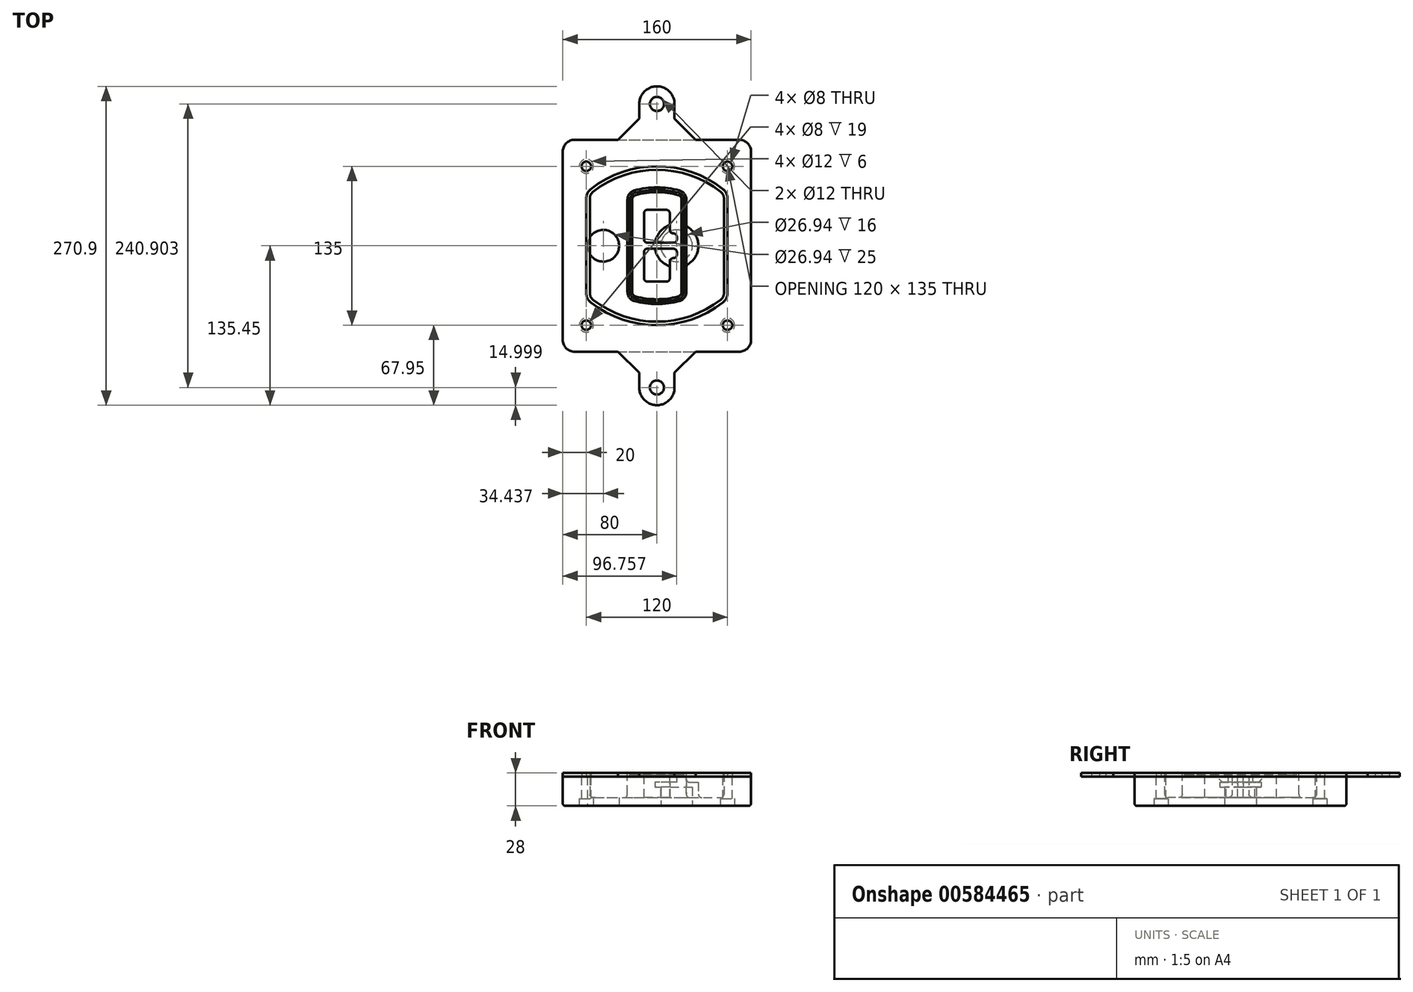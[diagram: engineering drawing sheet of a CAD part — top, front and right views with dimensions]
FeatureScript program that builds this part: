
annotation { "Feature Type Name" : "Feature", "Feature Type Description" : "" }
export const myFeature = defineFeature(function(context is Context, id is Id, definition is map)
    precondition{}
    {
        {
            var Q0;
            Q0=qCreatedBy(makeId("Top.planeOp"),FACE);
            var sketch = newSketch(context, id + "F0", { "sketchPlane" : qUnion([Q0])});
            skPoint(sketch, "E0.rect.middle", {"position": v(0, 0) * mm});
            skLineSegment(sketch, "E1.bottom", {"start": v(-70, -90) * mm, "end": v(70, -90) * mm});
            skLineSegment(sketch, "E1.top", {"start": v(-70, 90) * mm, "end": v(70, 90) * mm});
            skLineSegment(sketch, "E1.left", {"start": v(-80, -80) * mm, "end": v(-80, 80) * mm});
            skLineSegment(sketch, "E1.right", {"start": v(80, -80) * mm, "end": v(80, 80) * mm});
            skLineSegment(sketch, "E2", {"start": v(-80, 90) * mm, "end": v(80, -90) * mm, "construction": true});
            skLineSegment(sketch, "E3", {"start": v(80, 90) * mm, "end": v(-80, -90) * mm, "construction": true});
            skCircle(sketch, "E4", {"center": v(-60, 67.5) * mm, "radius": 4 * mm});
            skCircle(sketch, "E5", {"center": v(60, 67.5) * mm, "radius": 4 * mm});
            skCircle(sketch, "E6", {"center": v(60, -67.5) * mm, "radius": 4 * mm});
            skCircle(sketch, "E7", {"center": v(-60, -67.5) * mm, "radius": 4 * mm});
            skLineSegment(sketch, "E8", {"start": v(-60, 67.5) * mm, "end": v(60, 67.5) * mm, "construction": true});
            skLineSegment(sketch, "E9", {"start": v(60, 67.5) * mm, "end": v(60, -67.5) * mm, "construction": true});
            skLineSegment(sketch, "E10", {"start": v(60, -67.5) * mm, "end": v(-60, -67.5) * mm, "construction": true});
            skLineSegment(sketch, "E11", {"start": v(-60, -67.5) * mm, "end": v(-60, 67.5) * mm, "construction": true});
            skLineSegment(sketch, "E12", {"start": v(-60, 40.3) * mm, "end": v(-60, -40.3) * mm});
            skLineSegment(sketch, "E13", {"start": v(60, 40.3) * mm, "end": v(60, -40.3) * mm});
            skArc(sketch, "E14", {"start": v(56.15, 48.18) * mm, "mid": v(0, 67.5) * mm, "end": v(-56.15, 48.18) * mm});
            skArc(sketch, "E15", {"start": v(-56.15, -48.18) * mm, "mid": v(0, -67.5) * mm, "end": v(56.15, -48.18) * mm});
            skLineSegment(sketch, "E16", {"start": v(-60, 0) * mm, "end": v(60, 0) * mm, "construction": true});
            skPoint(sketch, "E17.visualSharp", {"position": v(-60, -45) * mm});
            skArc(sketch, "E17.filletArc", {"start": v(-60, -40.3) * mm, "mid": v(-58.99, -44.68) * mm, "end": v(-56.15, -48.18) * mm});
            skPoint(sketch, "E18.visualSharp", {"position": v(-60, 45) * mm});
            skArc(sketch, "E18.filletArc", {"start": v(-56.15, 48.18) * mm, "mid": v(-58.99, 44.68) * mm, "end": v(-60, 40.3) * mm});
            skPoint(sketch, "E19.visualSharp", {"position": v(60, 45) * mm});
            skArc(sketch, "E19.filletArc", {"start": v(60, 40.3) * mm, "mid": v(58.99, 44.68) * mm, "end": v(56.15, 48.18) * mm});
            skPoint(sketch, "E20.visualSharp", {"position": v(60, -45) * mm});
            skArc(sketch, "E20.filletArc", {"start": v(56.15, -48.18) * mm, "mid": v(58.99, -44.68) * mm, "end": v(60, -40.3) * mm});
            skPoint(sketch, "E21.visualSharp", {"position": v(-80, 90) * mm});
            skArc(sketch, "E21.filletArc", {"start": v(-70, 90) * mm, "mid": v(-77.07, 87.07) * mm, "end": v(-80, 80) * mm});
            skPoint(sketch, "E22.visualSharp", {"position": v(80, 90) * mm});
            skArc(sketch, "E22.filletArc", {"start": v(80, 80) * mm, "mid": v(77.07, 87.07) * mm, "end": v(70, 90) * mm});
            skPoint(sketch, "E23.visualSharp", {"position": v(80, -90) * mm});
            skArc(sketch, "E23.filletArc", {"start": v(70, -90) * mm, "mid": v(77.07, -87.07) * mm, "end": v(80, -80) * mm});
            skPoint(sketch, "E24.visualSharp", {"position": v(-80, -90) * mm});
            skArc(sketch, "E24.filletArc", {"start": v(-80, -80) * mm, "mid": v(-77.07, -87.07) * mm, "end": v(-70, -90) * mm});
            skArc(sketch, "E25.0", {"start": v(57, 40.3) * mm, "mid": v(56.3, 43.36) * mm, "end": v(54.3, 45.81) * mm});
            skLineSegment(sketch, "E25.1", {"start": v(57, 40.3) * mm, "end": v(57, -40.3) * mm});
            skArc(sketch, "E25.2", {"start": v(54.3, -45.81) * mm, "mid": v(56.3, -43.36) * mm, "end": v(57, -40.3) * mm});
            skArc(sketch, "E25.3", {"start": v(-54.3, -45.81) * mm, "mid": v(0, -64.5) * mm, "end": v(54.3, -45.81) * mm});
            skArc(sketch, "E25.4", {"start": v(-57, -40.3) * mm, "mid": v(-56.3, -43.36) * mm, "end": v(-54.3, -45.81) * mm});
            skArc(sketch, "E25.5", {"start": v(54.3, 45.81) * mm, "mid": v(0, 64.5) * mm, "end": v(-54.3, 45.81) * mm});
            skLineSegment(sketch, "E25.6", {"start": v(-57, 40.3) * mm, "end": v(-57, -40.3) * mm});
            skArc(sketch, "E25.7", {"start": v(-54.3, 45.81) * mm, "mid": v(-56.3, 43.36) * mm, "end": v(-57, 40.3) * mm});
            skArc(sketch, "E26.0", {"start": v(-58.62, 51.33) * mm, "mid": v(-62.58, 46.43) * mm, "end": v(-64, 40.3) * mm});
            skArc(sketch, "E26.1", {"start": v(58.62, 51.33) * mm, "mid": v(0, 71.5) * mm, "end": v(-58.62, 51.33) * mm});
            skArc(sketch, "E26.2", {"start": v(64, 40.3) * mm, "mid": v(62.58, 46.43) * mm, "end": v(58.62, 51.33) * mm});
            skLineSegment(sketch, "E26.3", {"start": v(64, 40.3) * mm, "end": v(64, -40.3) * mm});
            skArc(sketch, "E26.4", {"start": v(58.62, -51.33) * mm, "mid": v(62.58, -46.43) * mm, "end": v(64, -40.3) * mm});
            skLineSegment(sketch, "E26.5", {"start": v(-64, 40.3) * mm, "end": v(-64, -40.3) * mm});
            skArc(sketch, "E26.6", {"start": v(-58.62, -51.33) * mm, "mid": v(0, -71.5) * mm, "end": v(58.62, -51.33) * mm});
            skArc(sketch, "E26.7", {"start": v(-64, -40.3) * mm, "mid": v(-62.58, -46.43) * mm, "end": v(-58.62, -51.33) * mm});
            skSolve(sketch);
        }
        {
            var Q0;
            Q0=makeQuery(id+"F0.imprint","IMPRINT",FACE,{"disambiguationData":[TD([[makeQuery(id+"F0.imprint","IMPRINT",EDGE,{"derivedFrom":sQuery(id+"F0.wireOp",EDGE,"E1.bottom")}),1.0]])]});
            var Q1;
            Q1=makeQuery(id+"F0.imprint","IMPRINT",FACE,{"disambiguationData":[TD([[makeQuery(id+"F0.imprint","IMPRINT",EDGE,{"derivedFrom":sQuery(id+"F0.wireOp",EDGE,"E12")}),1.0]])]});
            var Q2;
            Q2=makeQuery(id+"F0.imprint","IMPRINT",FACE,{"disambiguationData":[TD([[makeQuery(id+"F0.imprint","IMPRINT",EDGE,{"derivedFrom":sQuery(id+"F0.wireOp",EDGE,"E25.0")}),1.0]])]});
            var Q3;
            Q3=makeQuery(id+"F0.imprint","IMPRINT",FACE,{"disambiguationData":[TD([[makeQuery(id+"F0.imprint","IMPRINT",EDGE,{"derivedFrom":sQuery(id+"F0.wireOp",EDGE,"E12")}),-1.0]])]});
            extrude(context, id + "F1", {"entities" : qUnion([Q0, Q1, Q2, Q3]), "oppositeDirection" : true, "depth" : 25 * mm});
        }
        {
            var Q0;
            Q0=makeQuery(id+"F0.imprint","IMPRINT",FACE,{"disambiguationData":[TD([[makeQuery(id+"F0.imprint","IMPRINT",EDGE,{"derivedFrom":sQuery(id+"F0.wireOp",EDGE,"E12")}),1.0]])]});
            extrude(context, id + "F2", {"entities" : qUnion([Q0]), "operationType" : NewBodyOperationType.ADD, "depth" : 3 * mm});
        }
        {
            var Q0;
            Q0=makeQuery(id+"F0.imprint","IMPRINT",FACE,{"disambiguationData":[TD([[makeQuery(id+"F0.imprint","IMPRINT",EDGE,{"derivedFrom":sQuery(id+"F0.wireOp",EDGE,"E25.0")}),1.0]])]});
            extrude(context, id + "F3", {"entities" : qUnion([Q0]), "operationType" : NewBodyOperationType.REMOVE, "oppositeDirection" : true, "depth" : 18 * mm});
        }
        {
            var Q0;
            Q0=makeQuery(id+"F2.opExtrude","CAP_FACE",FACE,{"disambiguationData":[OSD([sQuery(id+"F0.wireOp",EDGE,"E12"),sQuery(id+"F0.wireOp",EDGE,"E13"),sQuery(id+"F0.wireOp",EDGE,"E14"),sQuery(id+"F0.wireOp",EDGE,"E15"),sQuery(id+"F0.wireOp",EDGE,"E17.filletArc"),sQuery(id+"F0.wireOp",EDGE,"E18.filletArc"),sQuery(id+"F0.wireOp",EDGE,"E19.filletArc"),sQuery(id+"F0.wireOp",EDGE,"E20.filletArc"),sQuery(id+"F0.wireOp",EDGE,"E25.0"),sQuery(id+"F0.wireOp",EDGE,"E25.1"),sQuery(id+"F0.wireOp",EDGE,"E25.2"),sQuery(id+"F0.wireOp",EDGE,"E25.3"),sQuery(id+"F0.wireOp",EDGE,"E25.4"),sQuery(id+"F0.wireOp",EDGE,"E25.5"),sQuery(id+"F0.wireOp",EDGE,"E25.6"),sQuery(id+"F0.wireOp",EDGE,"E25.7")])],"isStart":false});
            var sketch = newSketch(context, id + "F4", { "sketchPlane" : qUnion([Q0])});
            skArc(sketch, "E27.0", {"start": v(-19.08, -46.97) * mm, "mid": v(0, -49.5) * mm, "end": v(19.08, -46.97) * mm});
            skArc(sketch, "E28.0", {"start": v(19.08, 46.97) * mm, "mid": v(0, 49.5) * mm, "end": v(-19.08, 46.97) * mm});
            skLineSegment(sketch, "E29", {"start": v(-25, 39.25) * mm, "end": v(-25, -39.25) * mm});
            skLineSegment(sketch, "E30", {"start": v(25, 39.25) * mm, "end": v(25, -39.25) * mm});
            skLineSegment(sketch, "E31", {"start": v(-25, 45.1) * mm, "end": v(25, 45.1) * mm, "construction": true});
            skLineSegment(sketch, "E32", {"start": v(-25, -45.1) * mm, "end": v(25, -45.1) * mm, "construction": true});
            skPoint(sketch, "E33.visualSharp", {"position": v(-25, 45.1) * mm});
            skArc(sketch, "E33.filletArc", {"start": v(-19.08, 46.97) * mm, "mid": v(-23.35, 44.11) * mm, "end": v(-25, 39.25) * mm});
            skPoint(sketch, "E34.visualSharp", {"position": v(25, 45.1) * mm});
            skArc(sketch, "E34.filletArc", {"start": v(25, 39.25) * mm, "mid": v(23.35, 44.11) * mm, "end": v(19.08, 46.97) * mm});
            skPoint(sketch, "E35.visualSharp", {"position": v(25, -45.1) * mm});
            skArc(sketch, "E35.filletArc", {"start": v(19.08, -46.97) * mm, "mid": v(23.35, -44.11) * mm, "end": v(25, -39.25) * mm});
            skPoint(sketch, "E36.visualSharp", {"position": v(-25, -45.1) * mm});
            skArc(sketch, "E36.filletArc", {"start": v(-25, -39.25) * mm, "mid": v(-23.35, -44.11) * mm, "end": v(-19.08, -46.97) * mm});
            skArc(sketch, "E37.0", {"start": v(54.3, 45.81) * mm, "mid": v(0, 64.5) * mm, "end": v(-54.3, 45.81) * mm});
            skArc(sketch, "E37.1", {"start": v(-54.3, 45.81) * mm, "mid": v(-56.3, 43.36) * mm, "end": v(-57, 40.3) * mm});
            skLineSegment(sketch, "E37.2", {"start": v(-57, 40.3) * mm, "end": v(-57, -40.3) * mm});
            skArc(sketch, "E37.3", {"start": v(-57, -40.3) * mm, "mid": v(-56.3, -43.36) * mm, "end": v(-54.3, -45.81) * mm});
            skArc(sketch, "E37.4", {"start": v(-54.3, -45.81) * mm, "mid": v(0, -64.5) * mm, "end": v(54.3, -45.81) * mm});
            skArc(sketch, "E37.5", {"start": v(54.3, -45.81) * mm, "mid": v(56.3, -43.36) * mm, "end": v(57, -40.3) * mm});
            skLineSegment(sketch, "E37.6", {"start": v(57, 40.3) * mm, "end": v(57, -40.3) * mm});
            skArc(sketch, "E37.7", {"start": v(57, 40.3) * mm, "mid": v(56.3, 43.36) * mm, "end": v(54.3, 45.81) * mm});
            skLineSegment(sketch, "E38.0", {"start": v(23, 39.25) * mm, "end": v(23, -39.25) * mm});
            skArc(sketch, "E38.1", {"start": v(18.56, -45.04) * mm, "mid": v(21.76, -42.9) * mm, "end": v(23, -39.25) * mm});
            skArc(sketch, "E38.2", {"start": v(-18.56, -45.04) * mm, "mid": v(0, -47.5) * mm, "end": v(18.56, -45.04) * mm});
            skArc(sketch, "E38.3", {"start": v(-23, -39.25) * mm, "mid": v(-21.76, -42.9) * mm, "end": v(-18.56, -45.04) * mm});
            skLineSegment(sketch, "E38.4", {"start": v(-23, 39.25) * mm, "end": v(-23, -39.25) * mm});
            skArc(sketch, "E38.5", {"start": v(23, 39.25) * mm, "mid": v(21.76, 42.9) * mm, "end": v(18.56, 45.04) * mm});
            skArc(sketch, "E38.6", {"start": v(-18.56, 45.04) * mm, "mid": v(-21.76, 42.9) * mm, "end": v(-23, 39.25) * mm});
            skArc(sketch, "E38.7", {"start": v(18.56, 45.04) * mm, "mid": v(0, 47.5) * mm, "end": v(-18.56, 45.04) * mm});
            skArc(sketch, "E39.0", {"start": v(21, 39.25) * mm, "mid": v(20.18, 41.68) * mm, "end": v(18.04, 43.1) * mm});
            skLineSegment(sketch, "E39.1", {"start": v(21, 39.25) * mm, "end": v(21, -39.25) * mm});
            skArc(sketch, "E39.2", {"start": v(18.04, -43.1) * mm, "mid": v(20.18, -41.68) * mm, "end": v(21, -39.25) * mm});
            skArc(sketch, "E39.3", {"start": v(-18.04, -43.1) * mm, "mid": v(0, -45.5) * mm, "end": v(18.04, -43.1) * mm});
            skArc(sketch, "E39.4", {"start": v(-21, -39.25) * mm, "mid": v(-20.18, -41.68) * mm, "end": v(-18.04, -43.1) * mm});
            skArc(sketch, "E39.5", {"start": v(18.04, 43.1) * mm, "mid": v(0, 45.5) * mm, "end": v(-18.04, 43.1) * mm});
            skLineSegment(sketch, "E39.6", {"start": v(-21, 39.25) * mm, "end": v(-21, -39.25) * mm});
            skArc(sketch, "E39.7", {"start": v(-18.04, 43.1) * mm, "mid": v(-20.18, 41.68) * mm, "end": v(-21, 39.25) * mm});
            skLineSegment(sketch, "E40", {"start": v(-25, 0) * mm, "end": v(25, 0) * mm, "construction": true});
            skLineSegment(sketch, "E41", {"start": v(-11, 5.5) * mm, "end": v(-11, 27.5) * mm});
            skLineSegment(sketch, "E42", {"start": v(-8, 30.5) * mm, "end": v(8, 30.5) * mm});
            skLineSegment(sketch, "E43", {"start": v(11, 27.5) * mm, "end": v(11, 13.5) * mm});
            skLineSegment(sketch, "E44", {"start": v(14, 10.5) * mm, "end": v(14, 10.5) * mm});
            skLineSegment(sketch, "E45", {"start": v(17, 7.5) * mm, "end": v(17, 5.5) * mm});
            skLineSegment(sketch, "E46", {"start": v(14, 2.5) * mm, "end": v(-8, 2.5) * mm});
            skPoint(sketch, "E47.visualSharp", {"position": v(-11, 30.5) * mm});
            skArc(sketch, "E47.filletArc", {"start": v(-8, 30.5) * mm, "mid": v(-10.12, 29.62) * mm, "end": v(-11, 27.5) * mm});
            skPoint(sketch, "E48.visualSharp", {"position": v(11, 30.5) * mm});
            skArc(sketch, "E48.filletArc", {"start": v(11, 27.5) * mm, "mid": v(10.12, 29.62) * mm, "end": v(8, 30.5) * mm});
            skPoint(sketch, "E49.visualSharp", {"position": v(11, 10.5) * mm});
            skArc(sketch, "E49.filletArc", {"start": v(11, 13.5) * mm, "mid": v(11.88, 11.38) * mm, "end": v(14, 10.5) * mm});
            skPoint(sketch, "E50.visualSharp", {"position": v(17, 10.5) * mm});
            skArc(sketch, "E50.filletArc", {"start": v(17, 7.5) * mm, "mid": v(16.12, 9.62) * mm, "end": v(14, 10.5) * mm});
            skPoint(sketch, "E51.visualSharp", {"position": v(17, 2.5) * mm});
            skArc(sketch, "E51.filletArc", {"start": v(14, 2.5) * mm, "mid": v(16.12, 3.38) * mm, "end": v(17, 5.5) * mm});
            skPoint(sketch, "E52.visualSharp", {"position": v(-11, 2.5) * mm});
            skArc(sketch, "E52.filletArc", {"start": v(-11, 5.5) * mm, "mid": v(-10.12, 3.38) * mm, "end": v(-8, 2.5) * mm});
            skLineSegment(sketch, "E53.0.MirrorCS", {"start": v(14, -2.5) * mm, "end": v(-8, -2.5) * mm});
            skArc(sketch, "E54.0.MirrorCS", {"start": v(-11, -5.5) * mm, "mid": v(-10.12, -3.38) * mm, "end": v(-8, -2.5) * mm});
            skLineSegment(sketch, "E55.0.MirrorCS", {"start": v(-11, -5.5) * mm, "end": v(-11, -27.5) * mm});
            skArc(sketch, "E56.0.MirrorCS", {"start": v(-8, -30.5) * mm, "mid": v(-10.12, -29.62) * mm, "end": v(-11, -27.5) * mm});
            skLineSegment(sketch, "E57.0.MirrorCS", {"start": v(-8, -30.5) * mm, "end": v(8, -30.5) * mm});
            skArc(sketch, "E58.0.MirrorCS", {"start": v(11, -27.5) * mm, "mid": v(10.12, -29.62) * mm, "end": v(8, -30.5) * mm});
            skLineSegment(sketch, "E59.0.MirrorCS", {"start": v(11, -27.5) * mm, "end": v(11, -13.5) * mm});
            skArc(sketch, "E60.0.MirrorCS", {"start": v(11, -13.5) * mm, "mid": v(11.88, -11.38) * mm, "end": v(14, -10.5) * mm});
            skArc(sketch, "E61.0.MirrorCS", {"start": v(17, -7.5) * mm, "mid": v(16.12, -9.62) * mm, "end": v(14, -10.5) * mm});
            skLineSegment(sketch, "E62.0.MirrorCS", {"start": v(17, -7.5) * mm, "end": v(17, -5.5) * mm});
            skArc(sketch, "E63.0.MirrorCS", {"start": v(14, -2.5) * mm, "mid": v(16.12, -3.38) * mm, "end": v(17, -5.5) * mm});
            skSolve(sketch);
        }
        {
            var Q0;
            Q0=makeQuery(id+"F4.imprint","IMPRINT",FACE,{"disambiguationData":[TD([[makeQuery(id+"F4.imprint","IMPRINT",EDGE,{"derivedFrom":sQuery(id+"F4.wireOp",EDGE,"E27.0")}),1.0]])]});
            var Q1;
            Q1=makeQuery(id+"F4.imprint","IMPRINT",FACE,{"disambiguationData":[TD([[makeQuery(id+"F4.imprint","IMPRINT",EDGE,{"derivedFrom":sQuery(id+"F4.wireOp",EDGE,"E38.0")}),-1.0]])]});
            var Q2;
            Q2=makeQuery(id+"F4.imprint","IMPRINT",FACE,{"disambiguationData":[TD([[makeQuery(id+"F4.imprint","IMPRINT",EDGE,{"derivedFrom":sQuery(id+"F4.wireOp",EDGE,"E39.0")}),1.0]])]});
            extrude(context, id + "F5", {"entities" : qUnion([Q0, Q1, Q2]), "operationType" : NewBodyOperationType.ADD, "endBound" : BoundingType.UP_TO_NEXT, "oppositeDirection" : true, "depth" : 25 * mm});
        }
        {
            var Q0;
            Q0=makeQuery(id+"F4.imprint","IMPRINT",FACE,{"disambiguationData":[TD([[makeQuery(id+"F4.imprint","IMPRINT",EDGE,{"derivedFrom":sQuery(id+"F4.wireOp",EDGE,"E38.0")}),-1.0]])]});
            extrude(context, id + "F6", {"entities" : qUnion([Q0]), "operationType" : NewBodyOperationType.REMOVE, "oppositeDirection" : true, "depth" : 2 * mm});
        }
        {
            var Q0;
            Q0=makeQuery(id+"F1.opExtrude","CAP_FACE",FACE,{"disambiguationData":[OSD([sQuery(id+"F0.wireOp",EDGE,"E1.bottom"),sQuery(id+"F0.wireOp",EDGE,"E1.top"),sQuery(id+"F0.wireOp",EDGE,"E1.left"),sQuery(id+"F0.wireOp",EDGE,"E1.right"),sQuery(id+"F0.wireOp",EDGE,"E4"),sQuery(id+"F0.wireOp",EDGE,"E5"),sQuery(id+"F0.wireOp",EDGE,"E6"),sQuery(id+"F0.wireOp",EDGE,"E7"),sQuery(id+"F0.wireOp",EDGE,"E21.filletArc"),sQuery(id+"F0.wireOp",EDGE,"E22.filletArc"),sQuery(id+"F0.wireOp",EDGE,"E23.filletArc"),sQuery(id+"F0.wireOp",EDGE,"E24.filletArc")])],"isStart":false});
            var sketch = newSketch(context, id + "F7", { "sketchPlane" : qUnion([Q0])});
            skCircle(sketch, "E64", {"center": v(16.76, 0) * mm, "radius": 13.47 * mm});
            skCircle(sketch, "E65", {"center": v(-45.56, 0) * mm, "radius": 13.47 * mm});
            skLineSegment(sketch, "E66", {"start": v(80, 0) * mm, "end": v(-80, 0) * mm});
            skCircle(sketch, "E67", {"center": v(16.76, 0) * mm, "radius": 18.47 * mm});
            skCircle(sketch, "E68", {"center": v(60, -67.5) * mm, "radius": 6 * mm});
            skCircle(sketch, "E69", {"center": v(-60, -67.5) * mm, "radius": 6 * mm});
            skCircle(sketch, "E70", {"center": v(-60, 67.5) * mm, "radius": 6 * mm});
            skCircle(sketch, "E71", {"center": v(60, 67.5) * mm, "radius": 6 * mm});
            skSolve(sketch);
        }
        {
            var Q0;
            {var subQ1=sQuery(id+"F7.wireOp",EDGE,"E66");var subQ4=sQuery(id+"F7.wireOp",EDGE,"E64");var subQ6=makeQuery(id+"F7.imprint","INTERSECT",VERTEX,{"disambiguationData":[OD(0.0)],"derivedFrom":[subQ4,subQ1]});Q0=makeQuery(id+"F7.imprint","IMPRINT",FACE,{"disambiguationData":[TD([[makeQuery(id+"F7.imprint","IMPRINT",EDGE,{"disambiguationData":[TD([[subQ6,-1.0]])],"derivedFrom":subQ4}),-1.0]])]});}
            var Q1;
            {var subQ0=sQuery(id+"F7.wireOp",EDGE,"E66");var subQ1=sQuery(id+"F7.wireOp",EDGE,"E64");var subQ3=makeQuery(id+"F7.imprint","INTERSECT",VERTEX,{"disambiguationData":[OD(0.0)],"derivedFrom":[subQ1,subQ0]});Q1=makeQuery(id+"F7.imprint","IMPRINT",FACE,{"disambiguationData":[TD([[makeQuery(id+"F7.imprint","IMPRINT",EDGE,{"disambiguationData":[TD([[subQ3,-1.0]])],"derivedFrom":subQ1}),1.0]])]});}
            var Q2;
            {var subQ0=sQuery(id+"F7.wireOp",EDGE,"E66");var subQ1=sQuery(id+"F7.wireOp",EDGE,"E64");var subQ3=makeQuery(id+"F7.imprint","INTERSECT",VERTEX,{"disambiguationData":[OD(0.0)],"derivedFrom":[subQ1,subQ0]});Q2=makeQuery(id+"F7.imprint","IMPRINT",FACE,{"disambiguationData":[TD([[makeQuery(id+"F7.imprint","IMPRINT",EDGE,{"disambiguationData":[TD([[subQ3,1.0]])],"derivedFrom":subQ1}),1.0]])]});}
            var Q3;
            {var subQ1=sQuery(id+"F7.wireOp",EDGE,"E66");var subQ4=sQuery(id+"F7.wireOp",EDGE,"E64");var subQ6=makeQuery(id+"F7.imprint","INTERSECT",VERTEX,{"disambiguationData":[OD(0.0)],"derivedFrom":[subQ4,subQ1]});Q3=makeQuery(id+"F7.imprint","IMPRINT",FACE,{"disambiguationData":[TD([[makeQuery(id+"F7.imprint","IMPRINT",EDGE,{"disambiguationData":[TD([[subQ6,1.0]])],"derivedFrom":subQ4}),-1.0]])]});}
            extrude(context, id + "F8", {"entities" : qUnion([Q0, Q1, Q2, Q3]), "operationType" : NewBodyOperationType.ADD, "oppositeDirection" : true, "depth" : 20 * mm});
        }
        {
            var Q0;
            {var subQ0=sQuery(id+"F7.wireOp",EDGE,"E66");var subQ1=sQuery(id+"F7.wireOp",EDGE,"E64");var subQ3=makeQuery(id+"F7.imprint","INTERSECT",VERTEX,{"disambiguationData":[OD(0.0)],"derivedFrom":[subQ1,subQ0]});Q0=makeQuery(id+"F7.imprint","IMPRINT",FACE,{"disambiguationData":[TD([[makeQuery(id+"F7.imprint","IMPRINT",EDGE,{"disambiguationData":[TD([[subQ3,-1.0]])],"derivedFrom":subQ1}),1.0]])]});}
            var Q1;
            {var subQ0=sQuery(id+"F7.wireOp",EDGE,"E66");var subQ1=sQuery(id+"F7.wireOp",EDGE,"E64");var subQ3=makeQuery(id+"F7.imprint","INTERSECT",VERTEX,{"disambiguationData":[OD(0.0)],"derivedFrom":[subQ1,subQ0]});Q1=makeQuery(id+"F7.imprint","IMPRINT",FACE,{"disambiguationData":[TD([[makeQuery(id+"F7.imprint","IMPRINT",EDGE,{"disambiguationData":[TD([[subQ3,1.0]])],"derivedFrom":subQ1}),1.0]])]});}
            extrude(context, id + "F9", {"entities" : qUnion([Q0, Q1]), "operationType" : NewBodyOperationType.REMOVE, "oppositeDirection" : true, "depth" : 16 * mm});
        }
        {
            var Q0;
            {var subQ0=sQuery(id+"F7.wireOp",EDGE,"E66");var subQ1=sQuery(id+"F7.wireOp",EDGE,"E65");var subQ3=makeQuery(id+"F7.imprint","INTERSECT",VERTEX,{"disambiguationData":[OD(0.0)],"derivedFrom":[subQ1,subQ0]});Q0=makeQuery(id+"F7.imprint","IMPRINT",FACE,{"disambiguationData":[TD([[makeQuery(id+"F7.imprint","IMPRINT",EDGE,{"disambiguationData":[TD([[subQ3,-1.0]])],"derivedFrom":subQ1}),1.0]])]});}
            var Q1;
            {var subQ0=sQuery(id+"F7.wireOp",EDGE,"E66");var subQ1=sQuery(id+"F7.wireOp",EDGE,"E65");var subQ3=makeQuery(id+"F7.imprint","INTERSECT",VERTEX,{"disambiguationData":[OD(0.0)],"derivedFrom":[subQ1,subQ0]});Q1=makeQuery(id+"F7.imprint","IMPRINT",FACE,{"disambiguationData":[TD([[makeQuery(id+"F7.imprint","IMPRINT",EDGE,{"disambiguationData":[TD([[subQ3,1.0]])],"derivedFrom":subQ1}),1.0]])]});}
            extrude(context, id + "F10", {"entities" : qUnion([Q0, Q1]), "operationType" : NewBodyOperationType.REMOVE, "oppositeDirection" : true, "depth" : 25 * mm});
        }
        {
            var Q0;
            Q0=makeQuery(id+"F7.imprint","IMPRINT",FACE,{"disambiguationData":[TD([[makeQuery(id+"F7.imprint","IMPRINT",EDGE,{"derivedFrom":sQuery(id+"F7.wireOp",EDGE,"E68")}),1.0]])]});
            var Q1;
            Q1=makeQuery(id+"F7.imprint","IMPRINT",FACE,{"disambiguationData":[TD([[makeQuery(id+"F7.imprint","IMPRINT",EDGE,{"derivedFrom":makeQuery(id+"F1.opExtrude","CAP_EDGE",EDGE,{"disambiguationData":[OSD([sQuery(id+"F0.wireOp",EDGE,"E5")])],"isStart":false})}),-1.0]])]});
            var Q2;
            Q2=makeQuery(id+"F7.imprint","IMPRINT",FACE,{"disambiguationData":[TD([[makeQuery(id+"F7.imprint","IMPRINT",EDGE,{"derivedFrom":sQuery(id+"F7.wireOp",EDGE,"E69")}),1.0]])]});
            var Q3;
            Q3=makeQuery(id+"F7.imprint","IMPRINT",FACE,{"disambiguationData":[TD([[makeQuery(id+"F7.imprint","IMPRINT",EDGE,{"derivedFrom":makeQuery(id+"F1.opExtrude","CAP_EDGE",EDGE,{"disambiguationData":[OSD([sQuery(id+"F0.wireOp",EDGE,"E4")])],"isStart":false})}),-1.0]])]});
            var Q4;
            Q4=makeQuery(id+"F7.imprint","IMPRINT",FACE,{"disambiguationData":[TD([[makeQuery(id+"F7.imprint","IMPRINT",EDGE,{"derivedFrom":sQuery(id+"F7.wireOp",EDGE,"E70")}),1.0]])]});
            var Q5;
            Q5=makeQuery(id+"F7.imprint","IMPRINT",FACE,{"disambiguationData":[TD([[makeQuery(id+"F7.imprint","IMPRINT",EDGE,{"derivedFrom":makeQuery(id+"F1.opExtrude","CAP_EDGE",EDGE,{"disambiguationData":[OSD([sQuery(id+"F0.wireOp",EDGE,"E7")])],"isStart":false})}),-1.0]])]});
            var Q6;
            Q6=makeQuery(id+"F7.imprint","IMPRINT",FACE,{"disambiguationData":[TD([[makeQuery(id+"F7.imprint","IMPRINT",EDGE,{"derivedFrom":sQuery(id+"F7.wireOp",EDGE,"E71")}),1.0]])]});
            var Q7;
            Q7=makeQuery(id+"F7.imprint","IMPRINT",FACE,{"disambiguationData":[TD([[makeQuery(id+"F7.imprint","IMPRINT",EDGE,{"derivedFrom":makeQuery(id+"F1.opExtrude","CAP_EDGE",EDGE,{"disambiguationData":[OSD([sQuery(id+"F0.wireOp",EDGE,"E6")])],"isStart":false})}),-1.0]])]});
            extrude(context, id + "F11", {"entities" : qUnion([Q0, Q1, Q2, Q3, Q4, Q5, Q6, Q7]), "operationType" : NewBodyOperationType.REMOVE, "oppositeDirection" : true, "depth" : 6 * mm});
        }
        {
            var Q0;
            Q0=makeQuery(id+"F9.boolean.opBoolean","COPY",FACE,{"derivedFrom":makeQuery(id+"F9.opExtrude","CAP_FACE",FACE,{"disambiguationData":[OSD([sQuery(id+"F7.wireOp",EDGE,"E64")])],"isStart":false})});
            var sketch = newSketch(context, id + "F12", { "sketchPlane" : qUnion([Q0])});
            skArc(sketch, "E72.0", {"start": v(11, 17.55) * mm, "mid": v(2.57, 11.82) * mm, "end": v(-1.54, 2.5) * mm});
            skArc(sketch, "E72.1", {"start": v(-1.54, -2.5) * mm, "mid": v(2.57, -11.82) * mm, "end": v(11, -17.55) * mm});
            skLineSegment(sketch, "E73", {"start": v(-1.54, -2.5) * mm, "end": v(14, -2.5) * mm});
            skLineSegment(sketch, "E74.0", {"start": v(14, 2.5) * mm, "end": v(-1.54, 2.5) * mm});
            skArc(sketch, "E74.1", {"start": v(14, 2.5) * mm, "mid": v(16.12, 3.38) * mm, "end": v(17, 5.5) * mm});
            skLineSegment(sketch, "E74.2", {"start": v(17, 7.5) * mm, "end": v(17, 5.5) * mm});
            skArc(sketch, "E74.3", {"start": v(17, 7.5) * mm, "mid": v(16.12, 9.62) * mm, "end": v(14, 10.5) * mm});
            skArc(sketch, "E74.4", {"start": v(11, 13.5) * mm, "mid": v(11.88, 11.38) * mm, "end": v(14, 10.5) * mm});
            skLineSegment(sketch, "E74.5", {"start": v(11, 17.55) * mm, "end": v(11, 13.5) * mm});
            skLineSegment(sketch, "E74.7", {"start": v(14, -2.5) * mm, "end": v(-1.54, -2.5) * mm});
            skArc(sketch, "E74.8", {"start": v(14, -2.5) * mm, "mid": v(16.12, -3.38) * mm, "end": v(17, -5.5) * mm});
            skLineSegment(sketch, "E74.9", {"start": v(17, -7.5) * mm, "end": v(17, -5.5) * mm});
            skArc(sketch, "E74.10", {"start": v(17, -7.5) * mm, "mid": v(16.12, -9.62) * mm, "end": v(14, -10.5) * mm});
            skArc(sketch, "E74.11", {"start": v(11, -13.5) * mm, "mid": v(11.88, -11.38) * mm, "end": v(14, -10.5) * mm});
            skLineSegment(sketch, "E74.12", {"start": v(11, -17.55) * mm, "end": v(11, -13.5) * mm});
            skPoint(sketch, "E75.orphan", {"position": v(11, -27.5) * mm});
            skPoint(sketch, "E76.orphan", {"position": v(-8, -2.5) * mm});
            skPoint(sketch, "E77.orphan", {"position": v(-8, 2.5) * mm});
            skPoint(sketch, "E78.orphan", {"position": v(11, 27.5) * mm});
            skSolve(sketch);
        }
        {
            var Q0;
            {var subQ7=sQuery(id+"F12.wireOp",EDGE,"E72.0");var subQ14=sQuery(id+"F12.wireOp",EDGE,"E72.1");var subQ16=sQuery(id+"F12.wireOp",EDGE,"E74.1");var subQ18=sQuery(id+"F12.wireOp",EDGE,"E74.8");Q0=qUnion([makeQuery(id+"F12.imprint","IMPRINT",FACE,{"disambiguationData":[TD([[makeQuery(id+"F12.imprint","IMPRINT",EDGE,{"derivedFrom":subQ7}),1.0]])]}),makeQuery(id+"F12.imprint","IMPRINT",FACE,{"disambiguationData":[TD([[makeQuery(id+"F12.imprint","IMPRINT",EDGE,{"derivedFrom":subQ14}),1.0]])]}),makeQuery(id+"F12.imprint","IMPRINT",FACE,{"disambiguationData":[TD([[makeQuery(id+"F12.imprint","IMPRINT",EDGE,{"derivedFrom":subQ16}),1.0]])]}),makeQuery(id+"F12.imprint","IMPRINT",FACE,{"disambiguationData":[TD([[makeQuery(id+"F12.imprint","IMPRINT",EDGE,{"derivedFrom":subQ18}),-1.0]])]})]);}
            var Q1;
            Q1=makeQuery(id+"F5.boolean.opBoolean","SPLIT",FACE,{"disambiguationData":[TD([makeQuery(id+"F5.opExtrude","SWEPT_FACE",FACE,{"disambiguationData":[OSD([sQuery(id+"F4.wireOp",EDGE,"E41")])]})])],"derivedFrom":makeQuery(id+"F3.boolean.opBoolean","COPY",FACE,{"derivedFrom":makeQuery(id+"F3.opExtrude","CAP_FACE",FACE,{"disambiguationData":[OSD([sQuery(id+"F0.wireOp",EDGE,"E25.0"),sQuery(id+"F0.wireOp",EDGE,"E25.1"),sQuery(id+"F0.wireOp",EDGE,"E25.2"),sQuery(id+"F0.wireOp",EDGE,"E25.3"),sQuery(id+"F0.wireOp",EDGE,"E25.4"),sQuery(id+"F0.wireOp",EDGE,"E25.5"),sQuery(id+"F0.wireOp",EDGE,"E25.6"),sQuery(id+"F0.wireOp",EDGE,"E25.7")])],"isStart":false})})});
            extrude(context, id + "F13", {"entities" : qUnion([Q0]), "operationType" : NewBodyOperationType.REMOVE, "endBound" : BoundingType.UP_TO_SURFACE, "endBoundEntityFace" : qUnion([Q1]), "depth" : 25 * mm});
        }
        {
            var Q0;
            Q0=makeQuery(id+"F3.boolean.opBoolean","COPY",EDGE,{"derivedFrom":makeQuery(id+"F3.opExtrude","CAP_EDGE",EDGE,{"disambiguationData":[OSD([sQuery(id+"F0.wireOp",EDGE,"E25.6")])],"isStart":false})});
            var Q1;
            Q1=makeQuery(id+"F8.boolean.opBoolean","INTERSECT",EDGE,{"derivedFrom":[makeQuery(id+"F5.opExtrude","SWEPT_FACE",FACE,{"disambiguationData":[OSD([sQuery(id+"F4.wireOp",EDGE,"E30")])]}),makeQuery(id+"F8.opExtrude","CAP_FACE",FACE,{"disambiguationData":[OSD([sQuery(id+"F7.wireOp",EDGE,"E67")])],"isStart":false})]});
            var Q2;
            Q2=makeQuery(id+"F8.boolean.opBoolean","INTERSECT",EDGE,{"disambiguationData":[OD(1.0)],"derivedFrom":[makeQuery(id+"F5.opExtrude","SWEPT_FACE",FACE,{"disambiguationData":[OSD([sQuery(id+"F4.wireOp",EDGE,"E30")])]}),makeQuery(id+"F8.opExtrude","SWEPT_FACE",FACE,{"disambiguationData":[OSD([sQuery(id+"F7.wireOp",EDGE,"E67")])]})]});
            var Q3;
            {var subQ0=sQuery(id+"F4.wireOp",EDGE,"E30");Q3=makeQuery(id+"F8.boolean.opBoolean","SPLIT",EDGE,{"disambiguationData":[TD([makeQuery(id+"F5.opExtrude","SWEPT_FACE",FACE,{"disambiguationData":[OSD([sQuery(id+"F4.wireOp",EDGE,"E35.filletArc")])]})])],"derivedFrom":makeQuery(id+"F5.opExtrude","CAP_EDGE",EDGE,{"disambiguationData":[OSD([subQ0])],"isStart":false})});}
            var Q4;
            {var subQ0=sQuery(id+"F0.wireOp",EDGE,"E25.7");var subQ1=sQuery(id+"F0.wireOp",EDGE,"E25.1");var subQ2=sQuery(id+"F0.wireOp",EDGE,"E25.6");var subQ3=sQuery(id+"F0.wireOp",EDGE,"E25.5");var subQ4=sQuery(id+"F0.wireOp",EDGE,"E25.4");var subQ5=sQuery(id+"F0.wireOp",EDGE,"E25.0");var subQ6=sQuery(id+"F0.wireOp",EDGE,"E25.2");var subQ7=sQuery(id+"F0.wireOp",EDGE,"E25.3");Q4=makeQuery(id+"F8.boolean.opBoolean","INTERSECT",EDGE,{"derivedFrom":[makeQuery(id+"F5.boolean.opBoolean","SPLIT",FACE,{"disambiguationData":[TD([makeQuery(id+"F2.opExtrude","SWEPT_FACE",FACE,{"disambiguationData":[OSD([subQ5])]})])],"derivedFrom":makeQuery(id+"F3.boolean.opBoolean","COPY",FACE,{"derivedFrom":makeQuery(id+"F3.opExtrude","CAP_FACE",FACE,{"disambiguationData":[OSD([subQ5,subQ1,subQ6,subQ7,subQ4,subQ3,subQ2,subQ0])],"isStart":false})})}),makeQuery(id+"F8.opExtrude","SWEPT_FACE",FACE,{"disambiguationData":[OSD([sQuery(id+"F7.wireOp",EDGE,"E67")])]})]});}
            var Q5;
            Q5=makeQuery(id+"F8.boolean.opBoolean","INTERSECT",EDGE,{"disambiguationData":[OD(0.0)],"derivedFrom":[makeQuery(id+"F5.opExtrude","SWEPT_FACE",FACE,{"disambiguationData":[OSD([sQuery(id+"F4.wireOp",EDGE,"E30")])]}),makeQuery(id+"F8.opExtrude","SWEPT_FACE",FACE,{"disambiguationData":[OSD([sQuery(id+"F7.wireOp",EDGE,"E67")])]})]});
            fillet(context, id + "F14", {"entities" : qUnion([Q0, Q1, Q2, Q3, Q4, Q5]), "radius" : 3 * mm, "tangentPropagation" : true, "allowEdgeOverflow" : false});
        }
        {
            var Q0;
            Q0=makeQuery(id+"F1.opExtrude","CAP_EDGE",EDGE,{"disambiguationData":[OSD([sQuery(id+"F0.wireOp",EDGE,"E1.bottom")])],"isStart":false});
            fillet(context, id + "F15", {"entities" : qUnion([Q0]), "radius" : 2 * mm, "tangentPropagation" : true, "allowEdgeOverflow" : false});
        }
        {
            var Q0;
            {var subQ0=sQuery(id+"F0.wireOp",EDGE,"E21.filletArc");var subQ1=sQuery(id+"F0.wireOp",EDGE,"E7");var subQ2=sQuery(id+"F0.wireOp",EDGE,"E6");var subQ3=sQuery(id+"F0.wireOp",EDGE,"E5");var subQ4=sQuery(id+"F0.wireOp",EDGE,"E4");var subQ5=sQuery(id+"F0.wireOp",EDGE,"E22.filletArc");var subQ6=sQuery(id+"F0.wireOp",EDGE,"E1.bottom");var subQ7=sQuery(id+"F0.wireOp",EDGE,"E1.right");var subQ8=sQuery(id+"F0.wireOp",EDGE,"E1.top");var subQ9=sQuery(id+"F0.wireOp",EDGE,"E1.left");var subQ10=sQuery(id+"F0.wireOp",EDGE,"E23.filletArc");var subQ11=sQuery(id+"F0.wireOp",EDGE,"E24.filletArc");Q0=makeQuery(id+"F2.boolean.opBoolean","SPLIT",FACE,{"disambiguationData":[TD([makeQuery(id+"F1.opExtrude","SWEPT_FACE",FACE,{"disambiguationData":[OSD([subQ6])]})])],"derivedFrom":makeQuery(id+"F1.opExtrude","CAP_FACE",FACE,{"disambiguationData":[OSD([subQ6,subQ8,subQ9,subQ7,subQ4,subQ3,subQ2,subQ1,subQ0,subQ5,subQ10,subQ11])],"isStart":true})});}
            var sketch = newSketch(context, id + "F16", { "sketchPlane" : qUnion([Q0])});
            skLineSegment(sketch, "E79.2", {"start": v(-80, -80) * mm, "end": v(-80, 80) * mm});
            skLineSegment(sketch, "E79.3", {"start": v(-70, 90) * mm, "end": v(-33, 90) * mm});
            skArc(sketch, "E79.4", {"start": v(80, 80) * mm, "mid": v(77.07, 87.07) * mm, "end": v(70, 90) * mm});
            skLineSegment(sketch, "E79.5", {"start": v(80, -80) * mm, "end": v(80, 80) * mm});
            skArc(sketch, "E79.6", {"start": v(70, -90) * mm, "mid": v(77.07, -87.07) * mm, "end": v(80, -80) * mm});
            skArc(sketch, "E79.7", {"start": v(-80, -80) * mm, "mid": v(-77.07, -87.07) * mm, "end": v(-70, -90) * mm});
            skPoint(sketch, "E79.8", {"position": v(-77.07, -87.07) * mm});
            skPoint(sketch, "E79.9", {"position": v(-77.07, 87.07) * mm});
            skPoint(sketch, "E79.10", {"position": v(77.07, 87.07) * mm});
            skCircle(sketch, "E80.0", {"center": v(-60, -67.5) * mm, "radius": 4 * mm});
            skCircle(sketch, "E80.1", {"center": v(60, -67.5) * mm, "radius": 4 * mm});
            skCircle(sketch, "E80.2", {"center": v(60, 67.5) * mm, "radius": 4 * mm});
            skCircle(sketch, "E80.3", {"center": v(-60, 67.5) * mm, "radius": 4 * mm});
            skArc(sketch, "E81.0", {"start": v(-56.15, -48.18) * mm, "mid": v(0, -67.5) * mm, "end": v(56.15, -48.18) * mm});
            skArc(sketch, "E81.1", {"start": v(56.15, -48.18) * mm, "mid": v(58.99, -44.68) * mm, "end": v(60, -40.3) * mm});
            skLineSegment(sketch, "E81.2", {"start": v(60, 40.3) * mm, "end": v(60, -40.3) * mm});
            skArc(sketch, "E81.3", {"start": v(60, 40.3) * mm, "mid": v(58.99, 44.68) * mm, "end": v(56.15, 48.18) * mm});
            skArc(sketch, "E81.4", {"start": v(56.15, 48.18) * mm, "mid": v(0, 67.5) * mm, "end": v(-56.15, 48.18) * mm});
            skArc(sketch, "E81.5", {"start": v(-60, -40.3) * mm, "mid": v(-58.99, -44.68) * mm, "end": v(-56.15, -48.18) * mm});
            skLineSegment(sketch, "E81.6", {"start": v(-60, 40.3) * mm, "end": v(-60, -40.3) * mm});
            skArc(sketch, "E81.7", {"start": v(-56.15, 48.18) * mm, "mid": v(-58.99, 44.68) * mm, "end": v(-60, 40.3) * mm});
            skLineSegment(sketch, "E82", {"start": v(-15, 108) * mm, "end": v(-15, 120) * mm});
            skArc(sketch, "E83", {"start": v(15, 120.45) * mm, "mid": v(-0.23, 135.45) * mm, "end": v(-15, 120) * mm});
            skLineSegment(sketch, "E84", {"start": v(15, 120.45) * mm, "end": v(15, 108) * mm});
            skLineSegment(sketch, "E85", {"start": v(15, 108) * mm, "end": v(33, 90) * mm});
            skCircle(sketch, "E86", {"center": v(0, 120.45) * mm, "radius": 6 * mm});
            skLineSegment(sketch, "E87", {"start": v(-80, 0) * mm, "end": v(80, 0) * mm, "construction": true});
            skLineSegment(sketch, "E88.trimOffspring", {"start": v(33, 90) * mm, "end": v(70, 90) * mm});
            skArc(sketch, "E89.0", {"start": v(-70, 90) * mm, "mid": v(-77.07, 87.07) * mm, "end": v(-80, 80) * mm});
            skLineSegment(sketch, "E90", {"start": v(-33, 90) * mm, "end": v(33, 90) * mm});
            skLineSegment(sketch, "E91", {"start": v(-33, 90) * mm, "end": v(-36.5, 90) * mm});
            skLineSegment(sketch, "E92", {"start": v(-15, 108) * mm, "end": v(-33, 90) * mm});
            skLineSegment(sketch, "E93", {"start": v(0, 120.45) * mm, "end": v(0, 90) * mm, "construction": true});
            skLineSegment(sketch, "E94", {"start": v(-70, -90) * mm, "end": v(70, -90) * mm});
            skLineSegment(sketch, "E95.MirrorCS", {"start": v(-33, -90) * mm, "end": v(-36.5, -90) * mm});
            skLineSegment(sketch, "E96.MirrorCS", {"start": v(-15, -108) * mm, "end": v(-15, -120) * mm});
            skCircle(sketch, "E97.MirrorC", {"center": v(0, -120.45) * mm, "radius": 6 * mm});
            skLineSegment(sketch, "E98.MirrorCS", {"start": v(-33, -90) * mm, "end": v(33, -90) * mm});
            skLineSegment(sketch, "E99.MirrorCS", {"start": v(15, -108) * mm, "end": v(33, -90) * mm});
            skArc(sketch, "E100.MirrorCS", {"start": v(15, -120.45) * mm, "mid": v(-0.23, -135.45) * mm, "end": v(-15, -120) * mm});
            skLineSegment(sketch, "E101.MirrorCS", {"start": v(0, -120.45) * mm, "end": v(0, -90) * mm, "construction": true});
            skLineSegment(sketch, "E102.MirrorCS", {"start": v(-15, -108) * mm, "end": v(-33, -90) * mm});
            skLineSegment(sketch, "E103.MirrorCS", {"start": v(15, -120.45) * mm, "end": v(15, -108) * mm});
            skSolve(sketch);
        }
        {
            var Q0;
            Q0 = qSketchRegion(id + "F16", true);
            var Q1;
            Q1=makeQuery(id+"F2.opExtrude","CAP_FACE",FACE,{"disambiguationData":[OSD([sQuery(id+"F0.wireOp",EDGE,"E12"),sQuery(id+"F0.wireOp",EDGE,"E13"),sQuery(id+"F0.wireOp",EDGE,"E14"),sQuery(id+"F0.wireOp",EDGE,"E15"),sQuery(id+"F0.wireOp",EDGE,"E17.filletArc"),sQuery(id+"F0.wireOp",EDGE,"E18.filletArc"),sQuery(id+"F0.wireOp",EDGE,"E19.filletArc"),sQuery(id+"F0.wireOp",EDGE,"E20.filletArc"),sQuery(id+"F0.wireOp",EDGE,"E25.0"),sQuery(id+"F0.wireOp",EDGE,"E25.1"),sQuery(id+"F0.wireOp",EDGE,"E25.2"),sQuery(id+"F0.wireOp",EDGE,"E25.3"),sQuery(id+"F0.wireOp",EDGE,"E25.4"),sQuery(id+"F0.wireOp",EDGE,"E25.5"),sQuery(id+"F0.wireOp",EDGE,"E25.6"),sQuery(id+"F0.wireOp",EDGE,"E25.7")])],"isStart":false});
            extrude(context, id + "F17", {"entities" : qUnion([Q0]), "endBound" : BoundingType.UP_TO_SURFACE, "depth" : 25 * mm, "endBoundEntityFace" : qUnion([Q1]), "offsetDistance" : 25 * mm});
        }
    });
